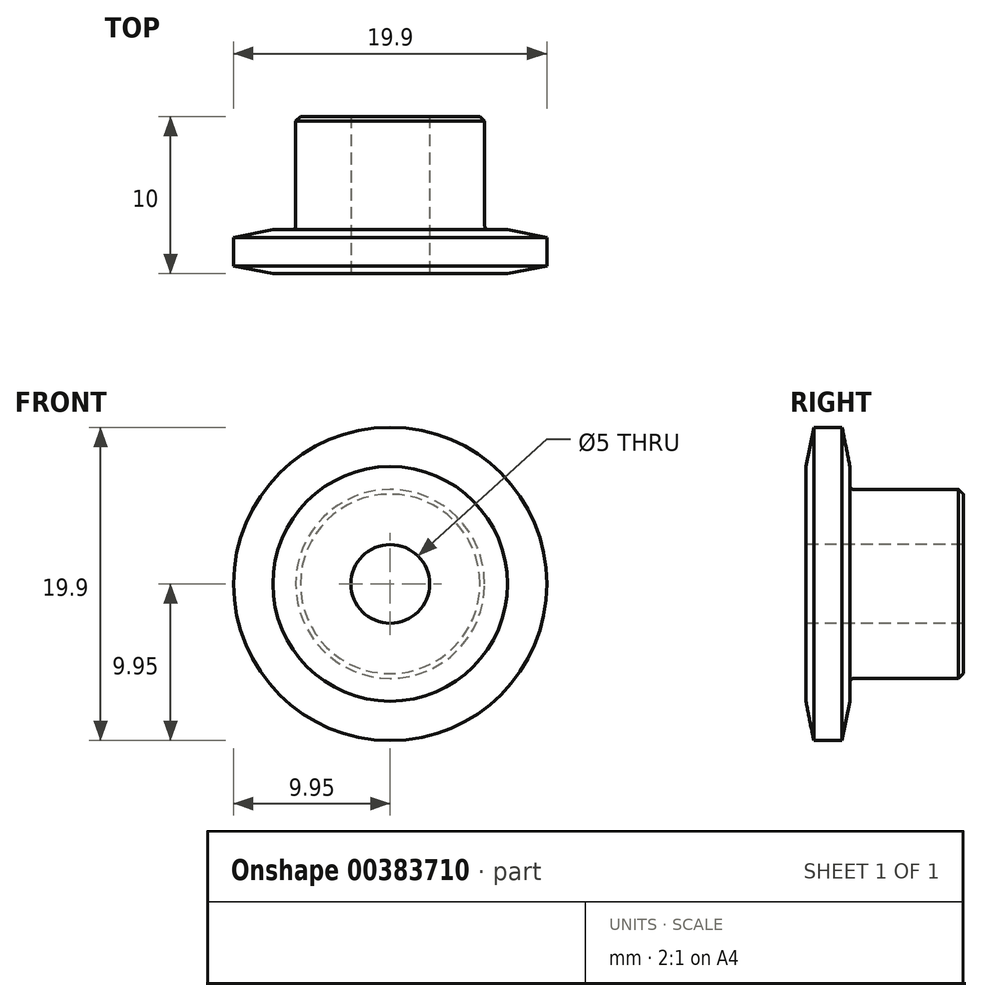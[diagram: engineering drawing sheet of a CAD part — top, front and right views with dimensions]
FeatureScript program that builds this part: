
annotation { "Feature Type Name" : "Feature", "Feature Type Description" : "" }
export const myFeature = defineFeature(function(context is Context, id is Id, definition is map)
    precondition{}
    {
        {
            var Q0;
            Q0=qCreatedBy(makeId("Right.planeOp"),FACE);
            var sketch = newSketch(context, id + "F0", { "sketchPlane" : qUnion([Q0])});
            skLineSegment(sketch, "E0", {"start": v(0, 2.5) * mm, "end": v(0, 9.95) * mm});
            skLineSegment(sketch, "E1", {"start": v(0, 9.95) * mm, "end": v(2.8, 9.95) * mm});
            skLineSegment(sketch, "E2", {"start": v(2.8, 9.95) * mm, "end": v(2.8, 6) * mm});
            skLineSegment(sketch, "E3", {"start": v(2.8, 6) * mm, "end": v(10, 6) * mm});
            skLineSegment(sketch, "E4", {"start": v(10, 6) * mm, "end": v(10, 2.5) * mm});
            skLineSegment(sketch, "E5", {"start": v(10, 2.5) * mm, "end": v(0, 2.5) * mm});
            skLineSegment(sketch, "E6", {"start": v(0, 0) * mm, "end": v(10.68, 0) * mm});
            skLineSegment(sketch, "E7.MirrorCS", {"start": v(0, -9.95) * mm, "end": v(2.8, -9.95) * mm});
            skLineSegment(sketch, "E8.MirrorCS", {"start": v(2.8, -9.95) * mm, "end": v(2.8, -6) * mm});
            skLineSegment(sketch, "E9.MirrorCS", {"start": v(10, -6) * mm, "end": v(10, -2.5) * mm});
            skLineSegment(sketch, "E10.MirrorCS", {"start": v(0, -2.5) * mm, "end": v(0, -9.95) * mm});
            skLineSegment(sketch, "E11.MirrorCS", {"start": v(10, -2.5) * mm, "end": v(0, -2.5) * mm});
            skLineSegment(sketch, "E12.MirrorCS", {"start": v(2.8, -6) * mm, "end": v(10, -6) * mm});
            skSolve(sketch);
        }
        {
            var Q0;
            Q0=makeQuery(id+"F0.imprint","IMPRINT",FACE,{"disambiguationData":[TD([[makeQuery(id+"F0.imprint","IMPRINT",EDGE,{"derivedFrom":sQuery(id+"F0.wireOp",EDGE,"E0")}),-1.0]])]});
            var Q1;
            Q1=sQuery(id+"F0.wireOp",EDGE,"E6");
            revolve(context, id + "F1", {"entities" : qUnion([Q0]), "axis" : qUnion([Q1]), "revolveType" : RevolveType.FULL});
        }
        {
            var Q0;
            Q0=makeQuery(id+"F1.opRevolve","SWEPT_EDGE",EDGE,{"disambiguationData":[OSD([sQuery(id+"F0.wireOp",EDGE,"E2"),sQuery(id+"F0.wireOp",EDGE,"E3")])]});
            fillet(context, id + "F2", {"entities" : qUnion([Q0]), "radius" : 0.25 * mm, "tangentPropagation" : true, "allowEdgeOverflow" : false});
        }
        {
            var Q0;
            Q0=makeQuery(id+"F1.opRevolve","SWEPT_EDGE",EDGE,{"disambiguationData":[OSD([sQuery(id+"F0.wireOp",EDGE,"E3"),sQuery(id+"F0.wireOp",EDGE,"E4")])]});
            chamfer(context, id + "F3", {"entities" : qUnion([Q0]), "width" : 0.3 * mm, "tangentPropagation" : true});
        }
        {
            var Q0;
            Q0=makeQuery(id+"F1.opRevolve","SWEPT_EDGE",EDGE,{"disambiguationData":[OSD([sQuery(id+"F0.wireOp",EDGE,"E0"),sQuery(id+"F0.wireOp",EDGE,"E1")])]});
            var Q1;
            Q1=makeQuery(id+"F1.opRevolve","SWEPT_EDGE",EDGE,{"disambiguationData":[OSD([sQuery(id+"F0.wireOp",EDGE,"E1"),sQuery(id+"F0.wireOp",EDGE,"E2")])]});
            chamfer(context, id + "F4", {"entities" : qUnion([Q0, Q1]), "chamferType" : ChamferType.TWO_OFFSETS, "width1" : 2.5 * mm, "oppositeDirection" : false, "width2" : .5 * mm, "tangentPropagation" : true});
        }
    });
